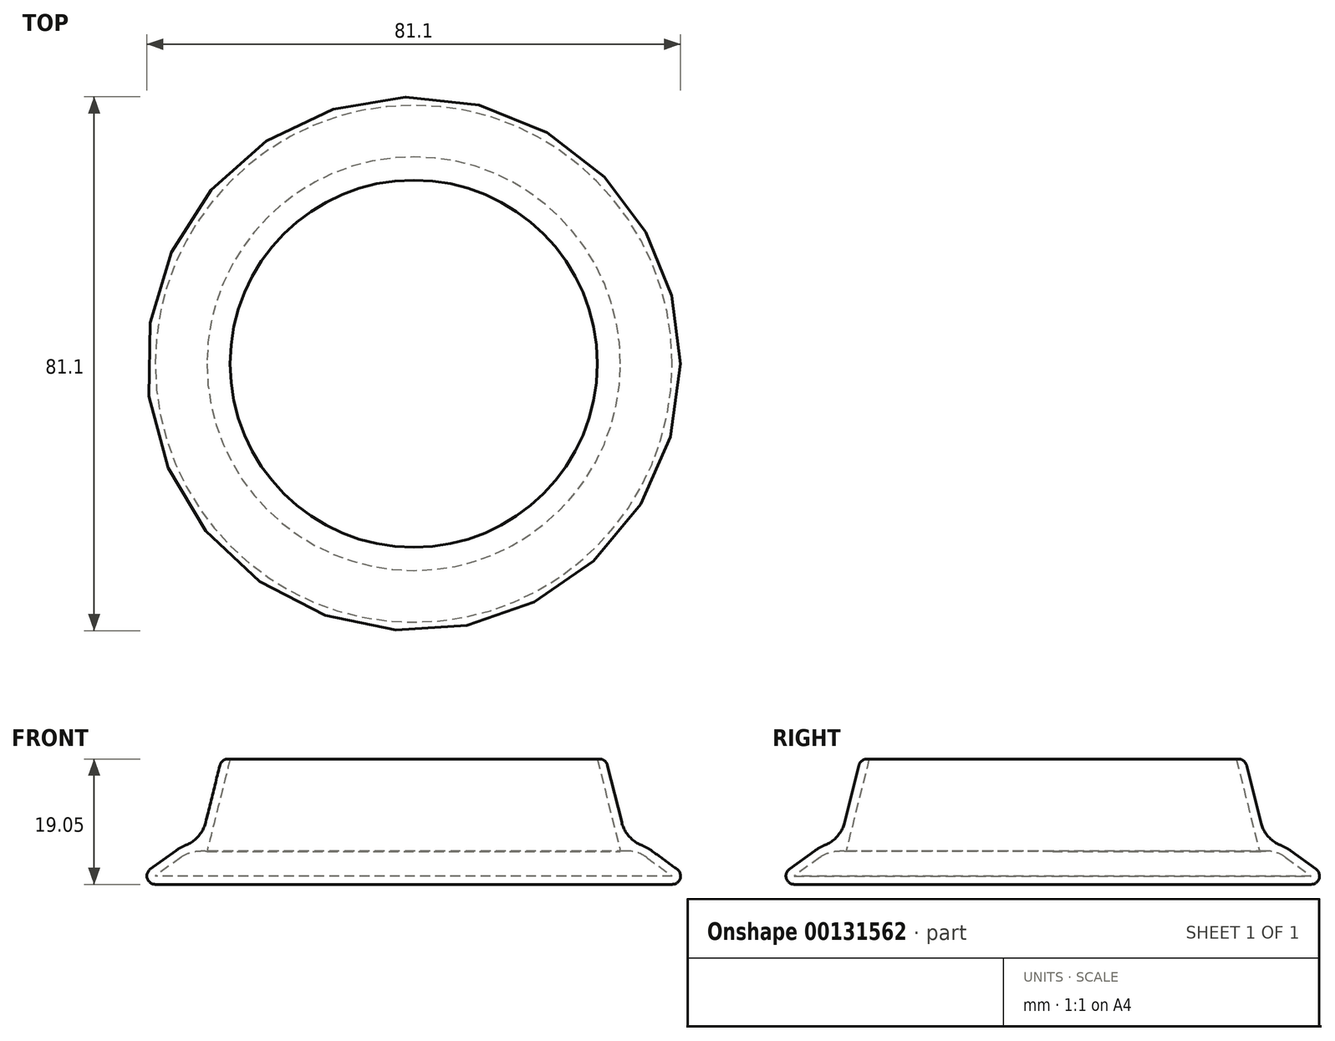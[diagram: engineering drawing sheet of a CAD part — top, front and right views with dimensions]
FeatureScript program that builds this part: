
annotation { "Feature Type Name" : "Feature", "Feature Type Description" : "" }
export const myFeature = defineFeature(function(context is Context, id is Id, definition is map)
    precondition{}
    {
        {
            var Q0;
            Q0=qCreatedBy(makeId("Front.planeOp"),FACE);
            var sketch = newSketch(context, id + "F0", { "sketchPlane" : qUnion([Q0])});
            skLineSegment(sketch, "E0", {"start": v(0, 0) * mm, "end": v(43.18, 0) * mm});
            skLineSegment(sketch, "E1", {"start": v(43.18, 0) * mm, "end": v(36.12, 5.14) * mm});
            skArc(sketch, "E2", {"start": v(36.12, 5.14) * mm, "mid": v(34.35, 6.04) * mm, "end": v(32.38, 6.35) * mm});
            skLineSegment(sketch, "E3", {"start": v(32.39, 6.35) * mm, "end": v(29.21, 19.05) * mm});
            skLineSegment(sketch, "E4", {"start": v(29.21, 19.05) * mm, "end": v(0, 19.05) * mm});
            skLineSegment(sketch, "E5", {"start": v(0, 19.05) * mm, "end": v(0, 0) * mm});
            skLineSegment(sketch, "E6", {"start": v(32.38, 6.35) * mm, "end": v(24.1, 6.35) * mm, "construction": true});
            skSolve(sketch);
        }
        {
            var Q0;
            Q0 = qSketchRegion(id + "F0", true);
            var Q1;
            Q1=sQuery(id+"F0.wireOp",EDGE,"E5");
            revolve(context, id + "F1", {"entities" : qUnion([Q0]), "axis" : qUnion([Q1]), "revolveType" : RevolveType.FULL});
        }
        {
            var Q0;
            Q0=makeQuery(id+"F1.opRevolve","SWEPT_FACE",FACE,{"disambiguationData":[OSD([sQuery(id+"F0.wireOp",EDGE,"E4")])]});
            shell(context, id + "F2", {"entities" : qUnion([Q0]), "thickness" : 1.27 * mm});
        }
        {
            var Q0;
            Q0=makeQuery(id+"F1.opRevolve","SWEPT_EDGE",EDGE,{"disambiguationData":[OSD([sQuery(id+"F0.wireOp",EDGE,"E0"),sQuery(id+"F0.wireOp",EDGE,"E1")])]});
            fillet(context, id + "F3", {"entities" : qUnion([Q0]), "radius" : 1.27 * mm, "tangentPropagation" : true, "allowEdgeOverflow" : false});
        }
        {
            var Q0;
            Q0=makeQuery(id+"F1.opRevolve","SWEPT_EDGE",EDGE,{"disambiguationData":[OSD([sQuery(id+"F0.wireOp",EDGE,"E3"),sQuery(id+"F0.wireOp",EDGE,"E4")])]});
            fillet(context, id + "F4", {"entities" : qUnion([Q0]), "radius" : 1.27 * mm, "tangentPropagation" : true, "allowEdgeOverflow" : false});
        }
        {
            var Q0;
            Q0=makeQuery(id+"F1.opRevolve","SWEPT_EDGE",EDGE,{"disambiguationData":[OSD([sQuery(id+"F0.wireOp",EDGE,"E2"),sQuery(id+"F0.wireOp",EDGE,"E3")])]});
            fillet(context, id + "F5", {"entities" : qUnion([Q0]), "radius" : 5.08 * mm, "tangentPropagation" : true, "allowEdgeOverflow" : false});
        }
    });
